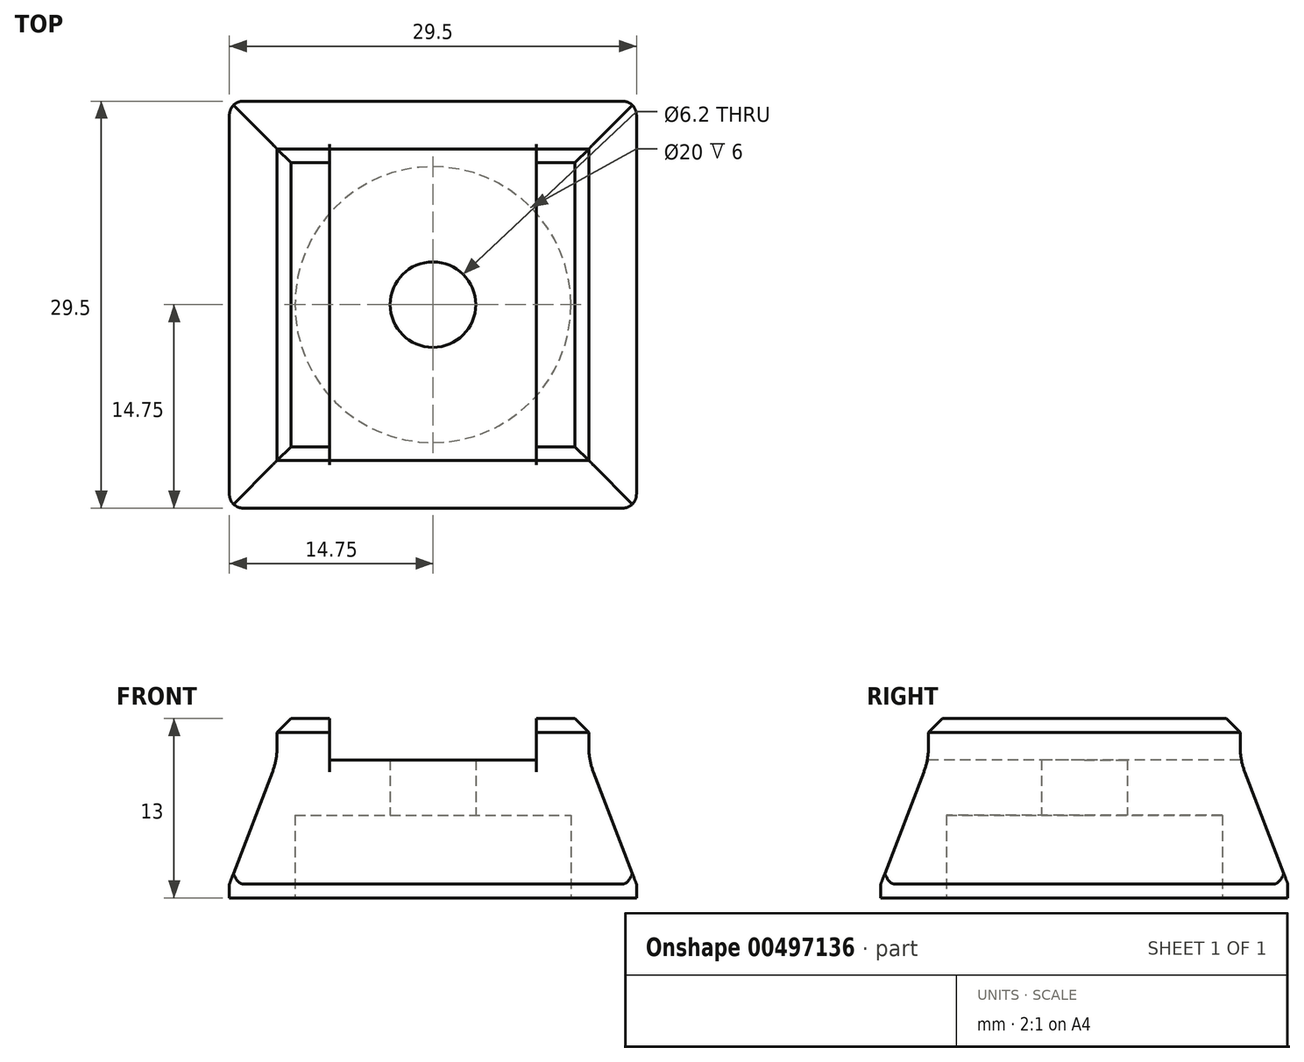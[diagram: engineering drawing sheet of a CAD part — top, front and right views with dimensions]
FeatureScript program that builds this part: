
annotation { "Feature Type Name" : "Feature", "Feature Type Description" : "" }
export const myFeature = defineFeature(function(context is Context, id is Id, definition is map)
    precondition{}
    {
        {
            var Q0;
            Q0=qCreatedBy(makeId("Top.planeOp"),FACE);
            var sketch = newSketch(context, id + "F0", { "sketchPlane" : qUnion([Q0])});
            skLineSegment(sketch, "E0.bottom", {"start": v(14.75, -14.75) * mm, "end": v(-14.75, -14.75) * mm});
            skLineSegment(sketch, "E0.top", {"start": v(14.75, 14.75) * mm, "end": v(-14.75, 14.75) * mm});
            skLineSegment(sketch, "E0.left", {"start": v(14.75, -14.75) * mm, "end": v(14.75, 14.75) * mm});
            skLineSegment(sketch, "E0.right", {"start": v(-14.75, -14.75) * mm, "end": v(-14.75, 14.75) * mm});
            skPoint(sketch, "E0.middle", {"position": v(0, 0) * mm});
            skSolve(sketch);
        }
        {
            var Q0;
            Q0=makeQuery(id+"F0.imprint","IMPRINT",FACE,{"disambiguationData":[TD([[makeQuery(id+"F0.imprint","IMPRINT",EDGE,{"derivedFrom":sQuery(id+"F0.wireOp",EDGE,"E0.bottom")}),-1.0]])]});
            extrude(context, id + "F1", {"entities" : qUnion([Q0]), "depth" : 9 * mm, "hasDraft" : true, "draftAngle" : 21 * degree, "draftPullDirection" : true});
        }
        {
            var Q0;
            Q0=makeQuery(id+"F1.opExtrude","CAP_FACE",FACE,{"disambiguationData":[OSD([sQuery(id+"F0.wireOp",EDGE,"E0.bottom"),sQuery(id+"F0.wireOp",EDGE,"E0.top"),sQuery(id+"F0.wireOp",EDGE,"E0.left"),sQuery(id+"F0.wireOp",EDGE,"E0.right")])],"isStart":true});
            var sketch = newSketch(context, id + "F2", { "sketchPlane" : qUnion([Q0])});
            skPoint(sketch, "E1", {"position": v(0, 0) * mm});
            skSolve(sketch);
        }
        {
            var Q0;
            Q0=sQuery(id+"F2.wireOp",VERTEX,"E1");
            var Q1;
            Q1=makeQuery(id+"F1.opExtrude","SWEPT_BODY",BODY,{"disambiguationData":[OSD([sQuery(id+"F0.wireOp",EDGE,"E0.bottom"),sQuery(id+"F0.wireOp",EDGE,"E0.top"),sQuery(id+"F0.wireOp",EDGE,"E0.left"),sQuery(id+"F0.wireOp",EDGE,"E0.right")])]});
            hole(context, id + "F3", {"style" : HoleStyle.C_BORE, "endStyle" : HoleEndStyle.THROUGH, "holeDiameter" : 6.2 * mm, "cBoreDiameter" : 20 * mm, "cBoreDepth" : 5 * mm, "isTappedThrough" : true, "tappedDepth" : 6.2 * mm, "tapClearance" : 3, "locations" : qUnion([Q0]), "scope" : qUnion([Q1])});
        }
        {
            var Q0;
            Q0=makeQuery(id+"F1.opExtrude","CAP_FACE",FACE,{"disambiguationData":[OSD([sQuery(id+"F0.wireOp",EDGE,"E0.bottom"),sQuery(id+"F0.wireOp",EDGE,"E0.top"),sQuery(id+"F0.wireOp",EDGE,"E0.left"),sQuery(id+"F0.wireOp",EDGE,"E0.right")])],"isStart":true});
            extrude(context, id + "F4", {"entities" : qUnion([Q0]), "operationType" : NewBodyOperationType.ADD, "depth" : 1 * mm});
        }
        {
            var Q0;
            Q0=makeQuery(id+"F4.opExtrude","SWEPT_EDGE",EDGE,{"disambiguationData":[OSD([sQuery(id+"F0.wireOp",EDGE,"E0.bottom"),sQuery(id+"F0.wireOp",EDGE,"E0.right")])]});
            var Q1;
            Q1=makeQuery(id+"F4.opExtrude","SWEPT_EDGE",EDGE,{"disambiguationData":[OSD([sQuery(id+"F0.wireOp",EDGE,"E0.bottom"),sQuery(id+"F0.wireOp",EDGE,"E0.left")])]});
            var Q2;
            Q2=makeQuery(id+"F4.opExtrude","SWEPT_EDGE",EDGE,{"disambiguationData":[OSD([sQuery(id+"F0.wireOp",EDGE,"E0.top"),sQuery(id+"F0.wireOp",EDGE,"E0.left")])]});
            var Q3;
            Q3=makeQuery(id+"F4.opExtrude","SWEPT_EDGE",EDGE,{"disambiguationData":[OSD([sQuery(id+"F0.wireOp",EDGE,"E0.top"),sQuery(id+"F0.wireOp",EDGE,"E0.right")])]});
            fillet(context, id + "F5", {"entities" : qUnion([Q0, Q1, Q2, Q3]), "radius" : 1 * mm, "tangentPropagation" : true, "allowEdgeOverflow" : false});
        }
        {
            var Q0;
            Q0=makeQuery(id+"F1.opExtrude","SWEPT_BODY",BODY,{"disambiguationData":[OSD([sQuery(id+"F0.wireOp",EDGE,"E0.bottom"),sQuery(id+"F0.wireOp",EDGE,"E0.top"),sQuery(id+"F0.wireOp",EDGE,"E0.left"),sQuery(id+"F0.wireOp",EDGE,"E0.right")])]});
            transform(context, id + "F6", {"entities" : qUnion([Q0]), "transformType" : TransformType.COPY});
        }
        {
            var Q0;
            Q0=makeQuery(id+"F6.opPattern","COPY",FACE,{"derivedFrom":makeQuery(id+"F1.opExtrude","CAP_FACE",FACE,{"disambiguationData":[OSD([sQuery(id+"F0.wireOp",EDGE,"E0.bottom"),sQuery(id+"F0.wireOp",EDGE,"E0.top"),sQuery(id+"F0.wireOp",EDGE,"E0.left"),sQuery(id+"F0.wireOp",EDGE,"E0.right")])],"isStart":false}),"instanceName":"1"});
            var sketch = newSketch(context, id + "F7", { "sketchPlane" : qUnion([Q0])});
            skLineSegment(sketch, "E2.bottom", {"start": v(-11.3, 11.3) * mm, "end": v(-7.5, 11.3) * mm});
            skLineSegment(sketch, "E2.top", {"start": v(-11.3, -11.3) * mm, "end": v(-7.5, -11.3) * mm});
            skLineSegment(sketch, "E2.left", {"start": v(-11.3, 11.3) * mm, "end": v(-11.3, -11.3) * mm});
            skLineSegment(sketch, "E2.right", {"start": v(-7.5, 11.3) * mm, "end": v(-7.5, -11.3) * mm});
            skLineSegment(sketch, "E3.bottom", {"start": v(7.5, 11.3) * mm, "end": v(11.3, 11.3) * mm});
            skLineSegment(sketch, "E3.top", {"start": v(7.5, -11.3) * mm, "end": v(11.3, -11.3) * mm});
            skLineSegment(sketch, "E3.left", {"start": v(7.5, 11.3) * mm, "end": v(7.5, -11.3) * mm});
            skLineSegment(sketch, "E3.right", {"start": v(11.3, 11.3) * mm, "end": v(11.3, -11.3) * mm});
            skSolve(sketch);
        }
        {
            var Q0;
            Q0=makeQuery(id+"F7.imprint","IMPRINT",FACE,{"disambiguationData":[TD([[makeQuery(id+"F7.imprint","IMPRINT",EDGE,{"derivedFrom":sQuery(id+"F7.wireOp",EDGE,"E2.bottom")}),1.0]])]});
            var Q1;
            Q1=makeQuery(id+"F7.imprint","IMPRINT",FACE,{"disambiguationData":[TD([[makeQuery(id+"F7.imprint","IMPRINT",EDGE,{"derivedFrom":sQuery(id+"F7.wireOp",EDGE,"E3.bottom")}),1.0]])]});
            extrude(context, id + "F8", {"entities" : qUnion([Q0, Q1]), "operationType" : NewBodyOperationType.ADD, "depth" : 3 * mm, "offsetDistance" : 25 * mm});
        }
        {
            var Q0;
            Q0=makeQuery(id+"F8.opExtrude","CAP_EDGE",EDGE,{"disambiguationData":[OSD([sQuery(id+"F7.wireOp",EDGE,"E3.top")])],"isStart":false});
            var Q1;
            Q1=makeQuery(id+"F8.opExtrude","CAP_EDGE",EDGE,{"disambiguationData":[OSD([sQuery(id+"F7.wireOp",EDGE,"E3.right")])],"isStart":false});
            var Q2;
            Q2=makeQuery(id+"F8.opExtrude","CAP_EDGE",EDGE,{"disambiguationData":[OSD([sQuery(id+"F7.wireOp",EDGE,"E2.left")])],"isStart":false});
            var Q3;
            Q3=makeQuery(id+"F8.opExtrude","CAP_EDGE",EDGE,{"disambiguationData":[OSD([sQuery(id+"F7.wireOp",EDGE,"E2.top")])],"isStart":false});
            var Q4;
            Q4=makeQuery(id+"F8.opExtrude","CAP_EDGE",EDGE,{"disambiguationData":[OSD([sQuery(id+"F7.wireOp",EDGE,"E2.bottom")])],"isStart":false});
            var Q5;
            Q5=makeQuery(id+"F8.opExtrude","CAP_EDGE",EDGE,{"disambiguationData":[OSD([sQuery(id+"F7.wireOp",EDGE,"E3.bottom")])],"isStart":false});
            chamfer(context, id + "F9", {"entities" : qUnion([Q0, Q1, Q2, Q3, Q4, Q5]), "width" : 1 * mm, "tangentPropagation" : true});
        }
        {
            var Q0;
            Q0=makeQuery(id+"F8.boolean.opBoolean","MERGE",EDGE,{"derivedFrom":[makeQuery(id+"F6.opPattern","COPY",EDGE,{"derivedFrom":makeQuery(id+"F1.opExtrude","CAP_EDGE",EDGE,{"disambiguationData":[OSD([sQuery(id+"F0.wireOp",EDGE,"E0.bottom")])],"isStart":false}),"instanceName":"1"}),makeQuery(id+"F8.opExtrude","CAP_EDGE",EDGE,{"disambiguationData":[OSD([sQuery(id+"F7.wireOp",EDGE,"E3.top")])],"isStart":true})]});
            var Q1;
            Q1=makeQuery(id+"F8.boolean.opBoolean","MERGE",EDGE,{"derivedFrom":[makeQuery(id+"F6.opPattern","COPY",EDGE,{"derivedFrom":makeQuery(id+"F1.opExtrude","CAP_EDGE",EDGE,{"disambiguationData":[OSD([sQuery(id+"F0.wireOp",EDGE,"E0.left")])],"isStart":false}),"instanceName":"1"}),makeQuery(id+"F8.opExtrude","CAP_EDGE",EDGE,{"disambiguationData":[OSD([sQuery(id+"F7.wireOp",EDGE,"E3.right")])],"isStart":true})]});
            var Q2;
            Q2=makeQuery(id+"F8.boolean.opBoolean","MERGE",EDGE,{"derivedFrom":[makeQuery(id+"F6.opPattern","COPY",EDGE,{"derivedFrom":makeQuery(id+"F1.opExtrude","CAP_EDGE",EDGE,{"disambiguationData":[OSD([sQuery(id+"F0.wireOp",EDGE,"E0.bottom")])],"isStart":false}),"instanceName":"1"}),makeQuery(id+"F8.opExtrude","CAP_EDGE",EDGE,{"disambiguationData":[OSD([sQuery(id+"F7.wireOp",EDGE,"E2.top")])],"isStart":true})]});
            var Q3;
            Q3=makeQuery(id+"F8.boolean.opBoolean","MERGE",EDGE,{"derivedFrom":[makeQuery(id+"F6.opPattern","COPY",EDGE,{"derivedFrom":makeQuery(id+"F1.opExtrude","CAP_EDGE",EDGE,{"disambiguationData":[OSD([sQuery(id+"F0.wireOp",EDGE,"E0.right")])],"isStart":false}),"instanceName":"1"}),makeQuery(id+"F8.opExtrude","CAP_EDGE",EDGE,{"disambiguationData":[OSD([sQuery(id+"F7.wireOp",EDGE,"E2.left")])],"isStart":true})]});
            var Q4;
            Q4=makeQuery(id+"F8.boolean.opBoolean","MERGE",EDGE,{"derivedFrom":[makeQuery(id+"F6.opPattern","COPY",EDGE,{"derivedFrom":makeQuery(id+"F1.opExtrude","CAP_EDGE",EDGE,{"disambiguationData":[OSD([sQuery(id+"F0.wireOp",EDGE,"E0.top")])],"isStart":false}),"instanceName":"1"}),makeQuery(id+"F8.opExtrude","CAP_EDGE",EDGE,{"disambiguationData":[OSD([sQuery(id+"F7.wireOp",EDGE,"E2.bottom")])],"isStart":true})]});
            var Q5;
            Q5=makeQuery(id+"F8.boolean.opBoolean","MERGE",EDGE,{"derivedFrom":[makeQuery(id+"F6.opPattern","COPY",EDGE,{"derivedFrom":makeQuery(id+"F1.opExtrude","CAP_EDGE",EDGE,{"disambiguationData":[OSD([sQuery(id+"F0.wireOp",EDGE,"E0.top")])],"isStart":false}),"instanceName":"1"}),makeQuery(id+"F8.opExtrude","CAP_EDGE",EDGE,{"disambiguationData":[OSD([sQuery(id+"F7.wireOp",EDGE,"E3.bottom")])],"isStart":true})]});
            fillet(context, id + "F10", {"entities" : qUnion([Q0, Q1, Q2, Q3, Q4, Q5]), "radius" : 5 * mm, "tangentPropagation" : true, "allowEdgeOverflow" : false});
        }
    });
